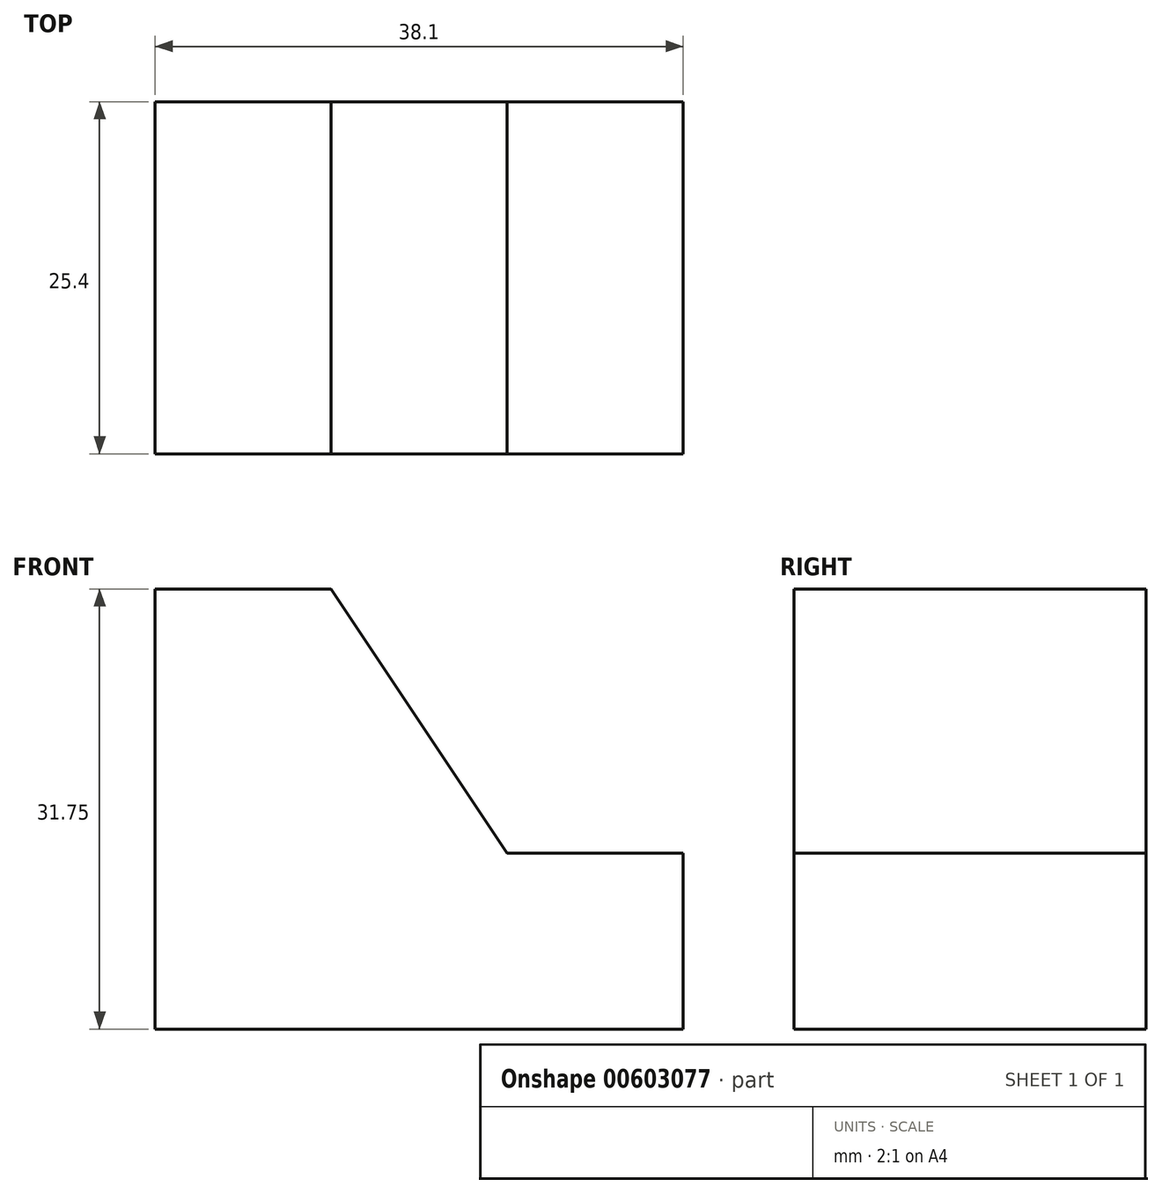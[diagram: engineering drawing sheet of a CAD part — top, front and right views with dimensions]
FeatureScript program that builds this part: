
annotation { "Feature Type Name" : "Feature", "Feature Type Description" : "" }
export const myFeature = defineFeature(function(context is Context, id is Id, definition is map)
    precondition{}
    {
        {
            var Q0;
            Q0=qCreatedBy(makeId("Front.planeOp"),FACE);
            var sketch = newSketch(context, id + "F0", { "sketchPlane" : qUnion([Q0])});
            skLineSegment(sketch, "E0", {"start": v(0, 0) * mm, "end": v(0, 31.75) * mm});
            skLineSegment(sketch, "E1", {"start": v(0, 31.75) * mm, "end": v(12.7, 31.75) * mm});
            skLineSegment(sketch, "E2", {"start": v(0, 0) * mm, "end": v(38.1, 0) * mm});
            skLineSegment(sketch, "E3", {"start": v(38.1, 0) * mm, "end": v(38.1, 12.7) * mm});
            skLineSegment(sketch, "E4", {"start": v(38.1, 12.7) * mm, "end": v(25.4, 12.7) * mm});
            skLineSegment(sketch, "E5", {"start": v(25.4, 12.7) * mm, "end": v(12.7, 31.75) * mm});
            skSolve(sketch);
        }
        {
            var Q0;
            Q0=makeQuery(id+"F0.imprint","IMPRINT",FACE,{"disambiguationData":[TD([[makeQuery(id+"F0.imprint","IMPRINT",EDGE,{"derivedFrom":sQuery(id+"F0.wireOp",EDGE,"E0")}),-1.0]])]});
            extrude(context, id + "F1", {"entities" : qUnion([Q0]), "depth" : 25.4 * mm, "offsetDistance" : 25.4 * mm});
        }
    });
